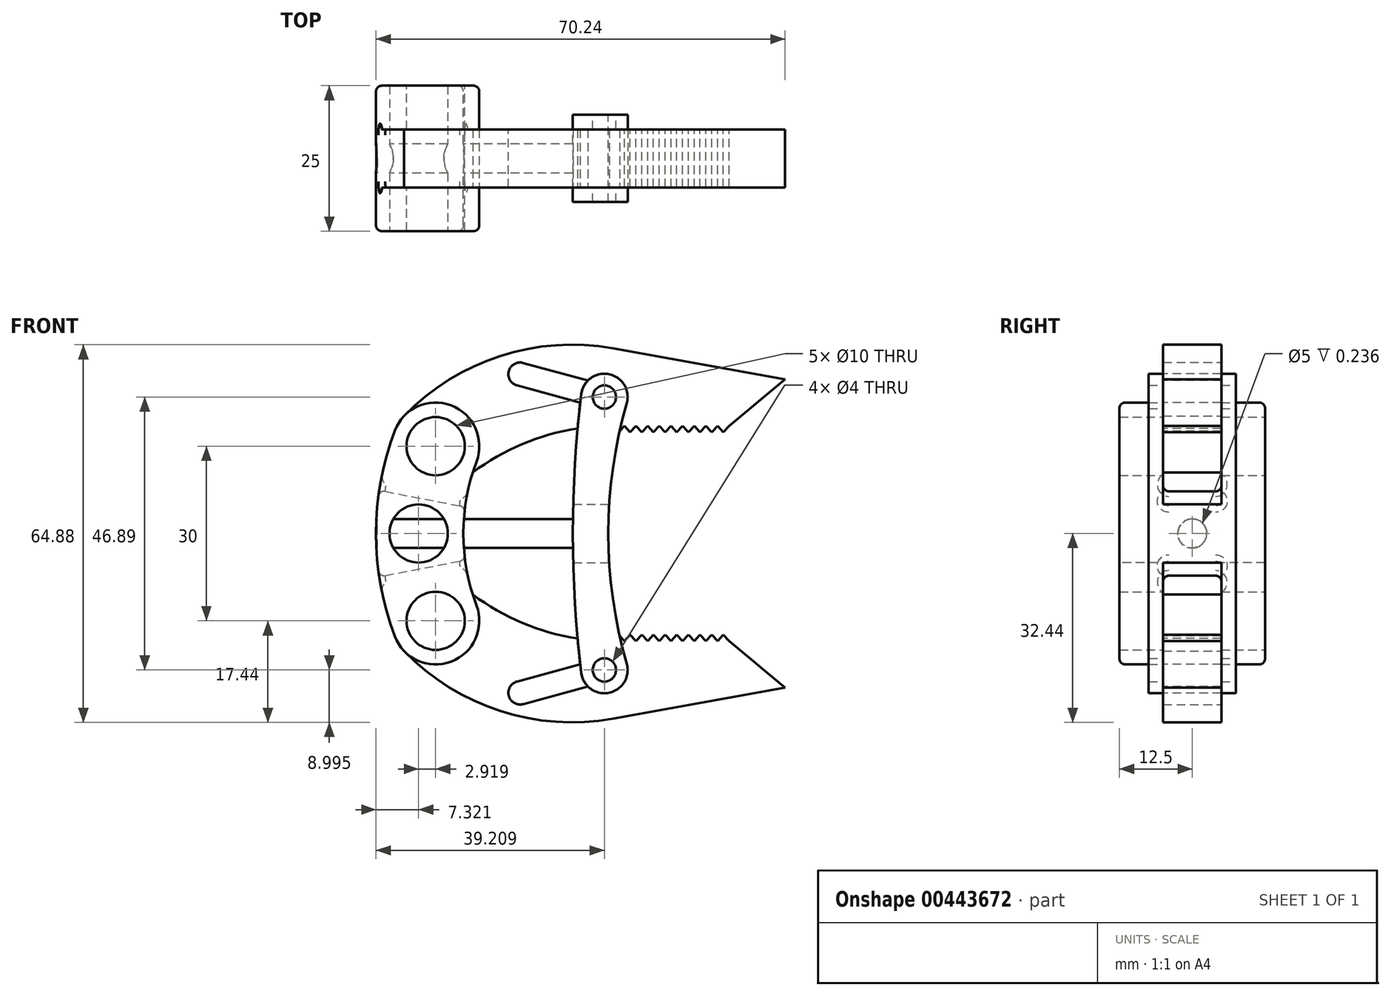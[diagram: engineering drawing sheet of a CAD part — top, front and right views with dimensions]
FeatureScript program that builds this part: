
annotation { "Feature Type Name" : "Feature", "Feature Type Description" : "" }
export const myFeature = defineFeature(function(context is Context, id is Id, definition is map)
    precondition{}
    {
        {
            var Q0;
            Q0=qCreatedBy(makeId("Front.planeOp"),FACE);
            var sketch = newSketch(context, id + "F0", { "sketchPlane" : qUnion([Q0])});
            skLineSegment(sketch, "E0", {"start": v(0, 15) * mm, "end": v(0, -15) * mm, "construction": true});
            skLineSegment(sketch, "E1", {"start": v(0, 0) * mm, "end": v(39.76, 0) * mm, "construction": true});
            skCircle(sketch, "E2", {"center": v(0, 15) * mm, "radius": 5 * mm});
            skCircle(sketch, "E3", {"center": v(0, -15) * mm, "radius": 5 * mm});
            skArc(sketch, "E4", {"start": v(-7.02, 17.65) * mm, "mid": v(-10.24, 0) * mm, "end": v(-7.02, -17.65) * mm});
            skCircle(sketch, "E5.0", {"center": v(0, 15) * mm, "radius": 7.5 * mm});
            skCircle(sketch, "E6.0", {"center": v(0, -15) * mm, "radius": 7.5 * mm});
            skArc(sketch, "E7", {"start": v(7.02, 12.35) * mm, "mid": v(4.76, 0) * mm, "end": v(7.02, -12.35) * mm});
            skSolve(sketch);
        }
        {
            var Q0;
            Q0=qCreatedBy(makeId("Front.planeOp"),FACE);
            var sketch = newSketch(context, id + "F1", { "sketchPlane" : qUnion([Q0])});
            skCircle(sketch, "E8.0", {"center": v(0, 15) * mm, "radius": 5 * mm});
            skArc(sketch, "E9", {"start": v(30.47, 31.81) * mm, "mid": v(11.08, 30.5) * mm, "end": v(-5.4, 20.2) * mm});
            skArc(sketch, "E10", {"start": v(30.4, 18.5) * mm, "mid": v(16.79, 16.12) * mm, "end": v(4.8, 9.24) * mm});
            skLineSegment(sketch, "E11", {"start": v(30.4, 18.5) * mm, "end": v(30.4, 18.5) * mm});
            skLineSegment(sketch, "E12", {"start": v(50.4, 18.5) * mm, "end": v(60, 26.5) * mm});
            skLineSegment(sketch, "E13", {"start": v(60, 26.5) * mm, "end": v(30.47, 31.81) * mm});
            skArc(sketch, "E14.0", {"start": v(-5.4, 20.2) * mm, "mid": v(-5.5, 9.9) * mm, "end": v(4.8, 9.24) * mm});
            skLineSegment(sketch, "E15", {"start": v(30.47, 31.81) * mm, "end": v(28.97, 23.45) * mm, "construction": true});
            skLineSegment(sketch, "E16", {"start": v(28.97, 23.45) * mm, "end": v(14.5, 27.38) * mm, "construction": true});
            skLineSegment(sketch, "E17", {"start": v(0, 0) * mm, "end": v(65.72, 0) * mm, "construction": true});
            skCircle(sketch, "E18", {"center": v(14.5, 27.38) * mm, "radius": 2 * mm});
            skCircle(sketch, "E19", {"center": v(28.97, 23.45) * mm, "radius": 2 * mm});
            skLineSegment(sketch, "E20", {"start": v(15.02, 29.3) * mm, "end": v(29.5, 25.38) * mm});
            skLineSegment(sketch, "E21", {"start": v(13.97, 25.45) * mm, "end": v(28.45, 21.51) * mm});
            skLineSegment(sketch, "E22", {"start": v(30.4, 18.5) * mm, "end": v(32.4, 18.5) * mm, "construction": true});
            skLineSegment(sketch, "E23", {"start": v(32.4, 18.5) * mm, "end": v(34.4, 18.5) * mm, "construction": true});
            skLineSegment(sketch, "E24", {"start": v(34.4, 18.5) * mm, "end": v(36.4, 18.5) * mm, "construction": true});
            skLineSegment(sketch, "E25", {"start": v(36.4, 18.5) * mm, "end": v(38.4, 18.5) * mm, "construction": true});
            skLineSegment(sketch, "E26", {"start": v(38.4, 18.5) * mm, "end": v(40.4, 18.5) * mm, "construction": true});
            skLineSegment(sketch, "E27", {"start": v(40.4, 18.5) * mm, "end": v(42.4, 18.5) * mm, "construction": true});
            skLineSegment(sketch, "E28", {"start": v(42.4, 18.5) * mm, "end": v(44.4, 18.5) * mm, "construction": true});
            skLineSegment(sketch, "E29", {"start": v(44.4, 18.5) * mm, "end": v(46.4, 18.5) * mm, "construction": true});
            skLineSegment(sketch, "E30", {"start": v(46.4, 18.5) * mm, "end": v(48.4, 18.5) * mm, "construction": true});
            skLineSegment(sketch, "E31", {"start": v(48.4, 18.5) * mm, "end": v(50.4, 18.5) * mm, "construction": true});
            skLineSegment(sketch, "E32", {"start": v(30.4, 18.5) * mm, "end": v(31.4, 17.39) * mm});
            skLineSegment(sketch, "E33", {"start": v(31.4, 17.39) * mm, "end": v(32.4, 18.5) * mm});
            skLineSegment(sketch, "E34", {"start": v(32.4, 18.5) * mm, "end": v(33.4, 17.39) * mm});
            skLineSegment(sketch, "E35", {"start": v(33.4, 17.39) * mm, "end": v(34.4, 18.5) * mm});
            skLineSegment(sketch, "E36", {"start": v(34.4, 18.5) * mm, "end": v(35.4, 17.39) * mm});
            skLineSegment(sketch, "E37", {"start": v(35.4, 17.39) * mm, "end": v(36.4, 18.5) * mm});
            skLineSegment(sketch, "E38", {"start": v(36.4, 18.5) * mm, "end": v(37.4, 17.39) * mm});
            skLineSegment(sketch, "E39", {"start": v(37.4, 17.39) * mm, "end": v(38.4, 18.5) * mm});
            skLineSegment(sketch, "E40", {"start": v(38.4, 18.5) * mm, "end": v(39.4, 17.39) * mm});
            skLineSegment(sketch, "E41", {"start": v(39.4, 17.39) * mm, "end": v(40.4, 18.5) * mm});
            skLineSegment(sketch, "E42", {"start": v(40.4, 18.5) * mm, "end": v(41.4, 17.39) * mm});
            skLineSegment(sketch, "E43", {"start": v(41.4, 17.39) * mm, "end": v(42.4, 18.5) * mm});
            skLineSegment(sketch, "E44", {"start": v(42.4, 18.5) * mm, "end": v(43.4, 17.39) * mm});
            skLineSegment(sketch, "E45", {"start": v(43.4, 17.39) * mm, "end": v(44.4, 18.5) * mm});
            skLineSegment(sketch, "E46", {"start": v(44.4, 18.5) * mm, "end": v(45.4, 17.39) * mm});
            skLineSegment(sketch, "E47", {"start": v(45.4, 17.39) * mm, "end": v(46.4, 18.5) * mm});
            skLineSegment(sketch, "E48", {"start": v(46.4, 18.5) * mm, "end": v(47.4, 17.39) * mm});
            skLineSegment(sketch, "E49", {"start": v(47.4, 17.39) * mm, "end": v(48.4, 18.5) * mm});
            skLineSegment(sketch, "E50", {"start": v(48.4, 18.5) * mm, "end": v(49.4, 17.39) * mm});
            skLineSegment(sketch, "E51", {"start": v(49.4, 17.39) * mm, "end": v(50.4, 18.5) * mm});
            skArc(sketch, "E52.MirrorCS", {"start": v(-5.4, -20.2) * mm, "mid": v(-5.5, -9.9) * mm, "end": v(4.8, -9.24) * mm});
            skLineSegment(sketch, "E53.MirrorCS", {"start": v(32.4, -18.5) * mm, "end": v(34.4, -18.5) * mm, "construction": true});
            skLineSegment(sketch, "E54.MirrorCS", {"start": v(30.4, -18.5) * mm, "end": v(32.4, -18.5) * mm, "construction": true});
            skLineSegment(sketch, "E55.MirrorCS", {"start": v(40.4, -18.5) * mm, "end": v(41.4, -17.39) * mm});
            skLineSegment(sketch, "E56.MirrorCS", {"start": v(44.4, -18.5) * mm, "end": v(46.4, -18.5) * mm, "construction": true});
            skLineSegment(sketch, "E57.MirrorCS", {"start": v(38.4, -18.5) * mm, "end": v(40.4, -18.5) * mm, "construction": true});
            skLineSegment(sketch, "E58.MirrorCS", {"start": v(46.4, -18.5) * mm, "end": v(48.4, -18.5) * mm, "construction": true});
            skLineSegment(sketch, "E59.MirrorCS", {"start": v(41.4, -17.39) * mm, "end": v(42.4, -18.5) * mm});
            skLineSegment(sketch, "E60.MirrorCS", {"start": v(36.4, -18.5) * mm, "end": v(38.4, -18.5) * mm, "construction": true});
            skLineSegment(sketch, "E61.MirrorCS", {"start": v(40.4, -18.5) * mm, "end": v(42.4, -18.5) * mm, "construction": true});
            skLineSegment(sketch, "E62.MirrorCS", {"start": v(34.4, -18.5) * mm, "end": v(36.4, -18.5) * mm, "construction": true});
            skLineSegment(sketch, "E63.MirrorCS", {"start": v(42.4, -18.5) * mm, "end": v(44.4, -18.5) * mm, "construction": true});
            skLineSegment(sketch, "E64.MirrorCS", {"start": v(30.4, -18.5) * mm, "end": v(31.4, -17.39) * mm});
            skLineSegment(sketch, "E65.MirrorCS", {"start": v(34.4, -18.5) * mm, "end": v(35.4, -17.39) * mm});
            skLineSegment(sketch, "E66.MirrorCS", {"start": v(38.4, -18.5) * mm, "end": v(39.4, -17.39) * mm});
            skLineSegment(sketch, "E67.MirrorCS", {"start": v(48.4, -18.5) * mm, "end": v(50.4, -18.5) * mm, "construction": true});
            skLineSegment(sketch, "E68.MirrorCS", {"start": v(32.4, -18.5) * mm, "end": v(33.4, -17.39) * mm});
            skLineSegment(sketch, "E69.MirrorCS", {"start": v(48.4, -18.5) * mm, "end": v(49.4, -17.39) * mm});
            skLineSegment(sketch, "E70.MirrorCS", {"start": v(44.4, -18.5) * mm, "end": v(45.4, -17.39) * mm});
            skLineSegment(sketch, "E71.MirrorCS", {"start": v(33.4, -17.39) * mm, "end": v(34.4, -18.5) * mm});
            skLineSegment(sketch, "E72.MirrorCS", {"start": v(31.4, -17.39) * mm, "end": v(32.4, -18.5) * mm});
            skLineSegment(sketch, "E73.MirrorCS", {"start": v(43.4, -17.39) * mm, "end": v(44.4, -18.5) * mm});
            skLineSegment(sketch, "E74.MirrorCS", {"start": v(35.4, -17.39) * mm, "end": v(36.4, -18.5) * mm});
            skLineSegment(sketch, "E75.MirrorCS", {"start": v(37.4, -17.39) * mm, "end": v(38.4, -18.5) * mm});
            skLineSegment(sketch, "E76.MirrorCS", {"start": v(45.4, -17.39) * mm, "end": v(46.4, -18.5) * mm});
            skLineSegment(sketch, "E77.MirrorCS", {"start": v(46.4, -18.5) * mm, "end": v(47.4, -17.39) * mm});
            skLineSegment(sketch, "E78.MirrorCS", {"start": v(39.4, -17.39) * mm, "end": v(40.4, -18.5) * mm});
            skLineSegment(sketch, "E79.MirrorCS", {"start": v(42.4, -18.5) * mm, "end": v(43.4, -17.39) * mm});
            skLineSegment(sketch, "E80.MirrorCS", {"start": v(49.4, -17.39) * mm, "end": v(50.4, -18.5) * mm});
            skLineSegment(sketch, "E81.MirrorCS", {"start": v(47.4, -17.39) * mm, "end": v(48.4, -18.5) * mm});
            skLineSegment(sketch, "E82.MirrorCS", {"start": v(36.4, -18.5) * mm, "end": v(37.4, -17.39) * mm});
            skLineSegment(sketch, "E83.MirrorCS", {"start": v(30.47, -31.81) * mm, "end": v(28.97, -23.45) * mm, "construction": true});
            skLineSegment(sketch, "E84.MirrorCS", {"start": v(28.97, -23.45) * mm, "end": v(14.5, -27.38) * mm, "construction": true});
            skCircle(sketch, "E85.MirrorC", {"center": v(14.5, -27.38) * mm, "radius": 2 * mm});
            skCircle(sketch, "E86.MirrorC", {"center": v(28.97, -23.45) * mm, "radius": 2 * mm});
            skLineSegment(sketch, "E87.MirrorCS", {"start": v(15.02, -29.3) * mm, "end": v(29.5, -25.38) * mm});
            skLineSegment(sketch, "E88.MirrorCS", {"start": v(13.97, -25.45) * mm, "end": v(28.45, -21.51) * mm});
            skCircle(sketch, "E89.MirrorC", {"center": v(0, -15) * mm, "radius": 5 * mm});
            skArc(sketch, "E90.MirrorCS", {"start": v(30.4, -18.5) * mm, "mid": v(16.79, -16.12) * mm, "end": v(4.8, -9.24) * mm});
            skLineSegment(sketch, "E91.MirrorCS", {"start": v(60, -26.5) * mm, "end": v(30.47, -31.81) * mm});
            skArc(sketch, "E92.MirrorCS", {"start": v(30.47, -31.81) * mm, "mid": v(11.08, -30.5) * mm, "end": v(-5.4, -20.2) * mm});
            skLineSegment(sketch, "E93.MirrorCS", {"start": v(50.4, -18.5) * mm, "end": v(60, -26.5) * mm});
            skSolve(sketch);
        }
        {
            var Q0;
            Q0 = qSketchRegion(id + "F0", true);
            extrude(context, id + "F2", {"entities" : qUnion([Q0]), "endBound" : BoundingType.SYMMETRIC, "depth" : 25 * mm});
        }
        {
            var Q0;
            Q0 = qSketchRegion(id + "F1", true);
            extrude(context, id + "F3", {"entities" : qUnion([Q0]), "endBound" : BoundingType.SYMMETRIC, "depth" : 10 * mm});
        }
        {
            var Q0;
            Q0=makeQuery(id+"F2.opExtrude","CAP_FACE",FACE,{"disambiguationData":[OSD([sQuery(id+"F0.wireOp",EDGE,"E2"),sQuery(id+"F0.wireOp",EDGE,"E3"),sQuery(id+"F0.wireOp",EDGE,"E4"),sQuery(id+"F0.wireOp",EDGE,"E5.0"),sQuery(id+"F0.wireOp",EDGE,"E6.0"),sQuery(id+"F0.wireOp",EDGE,"E7")])],"isStart":false});
            var sketch = newSketch(context, id + "F4", { "sketchPlane" : qUnion([Q0])});
            skCircle(sketch, "E94", {"center": v(0, 15) * mm, "radius": 5 * mm});
            skCircle(sketch, "E95", {"center": v(0, -15) * mm, "radius": 5 * mm});
            skArc(sketch, "E96", {"start": v(0, 15) * mm, "mid": v(-2.92, 0) * mm, "end": v(0, -15) * mm, "construction": true});
            skCircle(sketch, "E97", {"center": v(-2.92, 0) * mm, "radius": 5 * mm});
            skSolve(sketch);
        }
        {
            var Q0;
            Q0=makeQuery(id+"F4.imprint","IMPRINT",FACE,{"disambiguationData":[TD([[makeQuery(id+"F4.imprint","IMPRINT",EDGE,{"derivedFrom":sQuery(id+"F4.wireOp",EDGE,"E97")}),1.0]])]});
            extrude(context, id + "F5", {"entities" : qUnion([Q0]), "operationType" : NewBodyOperationType.REMOVE, "endBound" : BoundingType.THROUGH_ALL, "oppositeDirection" : true, "depth" : 25 * mm});
        }
        {
            var Q0;
            Q0=qCreatedBy(makeId("Front.planeOp"),FACE);
            var sketch = newSketch(context, id + "F6", { "sketchPlane" : qUnion([Q0])});
            skCircle(sketch, "E98", {"center": v(-2.92, 0) * mm, "radius": 5 * mm});
            skCircle(sketch, "E99", {"center": v(0, 15) * mm, "radius": 5 * mm});
            skCircle(sketch, "E100.0", {"center": v(-2.92, 0) * mm, "radius": 6 * mm, "construction": true});
            skCircle(sketch, "E101", {"center": v(0, 15) * mm, "radius": 9.28 * mm, "construction": true});
            skLineSegment(sketch, "E102", {"start": v(0, 15) * mm, "end": v(-2.92, 0) * mm, "construction": true});
            skLineSegment(sketch, "E103", {"start": v(-2.92, 0) * mm, "end": v(25, 0) * mm, "construction": true});
            skLineSegment(sketch, "E104", {"start": v(-9.68, 7.43) * mm, "end": v(5.06, 4.56) * mm});
            skLineSegment(sketch, "E105.MirrorCS", {"start": v(-9.68, -7.43) * mm, "end": v(5.06, -4.56) * mm});
            skArc(sketch, "E106", {"start": v(7.02, 12.35) * mm, "mid": v(5.82, 8.51) * mm, "end": v(5.06, 4.56) * mm});
            skArc(sketch, "E107", {"start": v(-7.02, 17.65) * mm, "mid": v(-8.62, 12.6) * mm, "end": v(-9.68, 7.43) * mm});
            skArc(sketch, "E108.MirrorCS", {"start": v(7.02, -12.35) * mm, "mid": v(5.82, -8.51) * mm, "end": v(5.06, -4.56) * mm});
            skArc(sketch, "E109.MirrorCS", {"start": v(-7.02, -17.65) * mm, "mid": v(-8.62, -12.6) * mm, "end": v(-9.68, -7.43) * mm});
            skArc(sketch, "E110", {"start": v(-7.02, -17.65) * mm, "mid": v(2.65, -22.02) * mm, "end": v(7.02, -12.35) * mm});
            skArc(sketch, "E111", {"start": v(7.02, 12.35) * mm, "mid": v(2.65, 22.02) * mm, "end": v(-7.02, 17.65) * mm});
            skSolve(sketch);
        }
        {
            var Q0;
            Q0 = qSketchRegion(id + "F6", true);
            var Q1;
            Q1=sQuery(id+"F6.wireOp",EDGE,"E104");
            var Q2;
            Q2=sQuery(id+"F6.wireOp",EDGE,"E107");
            var Q3;
            Q3=sQuery(id+"F6.wireOp",EDGE,"E111");
            var Q4;
            Q4=sQuery(id+"F6.wireOp",EDGE,"E106");
            var Q5;
            Q5=sQuery(id+"F6.wireOp",EDGE,"E108.MirrorCS");
            var Q6;
            Q6=sQuery(id+"F6.wireOp",EDGE,"E110");
            var Q7;
            Q7=sQuery(id+"F6.wireOp",EDGE,"E105.MirrorCS");
            var Q8;
            Q8=sQuery(id+"F6.wireOp",EDGE,"E109.MirrorCS");
            extrude(context, id + "F7", {"entities" : qUnion([Q0]), "operationType" : NewBodyOperationType.REMOVE, "surfaceEntities" : qUnion([Q1, Q2, Q3, Q4, Q5, Q6, Q7, Q8]), "endBound" : BoundingType.SYMMETRIC, "oppositeDirection" : true, "depth" : 10 * mm});
        }
        {
            var Q0;
            Q0=qCreatedBy(makeId("Right.planeOp"),FACE);
            var sketch = newSketch(context, id + "F8", { "sketchPlane" : qUnion([Q0])});
            skCircle(sketch, "E112", {"center": v(0, 0) * mm, "radius": 2.5 * mm});
            skSolve(sketch);
        }
        {
            var Q0;
            Q0 = qSketchRegion(id + "F8", true);
            extrude(context, id + "F9", {"entities" : qUnion([Q0]), "operationType" : NewBodyOperationType.REMOVE, "endBound" : BoundingType.THROUGH_ALL, "depth" : 25 * mm, "hasSecondDirection" : true, "secondDirectionBound" : SecondDirectionBoundingType.THROUGH_ALL, "secondDirectionOppositeDirection" : true, "secondDirectionDepth" : 25 * mm});
        }
        {
            var Q0;
            Q0 = qSketchRegion(id + "F8", true);
            extrude(context, id + "F10", {"entities" : qUnion([Q0]), "depth" : 27 * mm, "hasSecondDirection" : true, "secondDirectionOppositeDirection" : true, "secondDirectionDepth" : 10 * mm});
        }
        {
            var Q0;
            Q0=qCreatedBy(makeId("Front.planeOp"),FACE);
            var sketch = newSketch(context, id + "F11", { "sketchPlane" : qUnion([Q0])});
            skCircle(sketch, "E113", {"center": v(28.97, 23.45) * mm, "radius": 2 * mm});
            skCircle(sketch, "E114", {"center": v(28.97, -23.45) * mm, "radius": 2 * mm});
            skCircle(sketch, "E115", {"center": v(28.97, 23.45) * mm, "radius": 4 * mm});
            skCircle(sketch, "E116", {"center": v(28.97, -23.45) * mm, "radius": 4 * mm});
            skArc(sketch, "E117", {"start": v(32.81, 22.33) * mm, "mid": v(29.63, 0) * mm, "end": v(32.81, -22.33) * mm});
            skArc(sketch, "E118", {"start": v(25, 23.92) * mm, "mid": v(23.56, 0) * mm, "end": v(25, -23.92) * mm});
            skLineSegment(sketch, "E119", {"start": v(0.5, 0) * mm, "end": v(51.97, 0) * mm, "construction": true});
            skLineSegment(sketch, "E120", {"start": v(28.97, 23.45) * mm, "end": v(28.97, -23.45) * mm, "construction": true});
            skSolve(sketch);
        }
        {
            var Q0;
            Q0 = qSketchRegion(id + "F11", true);
            extrude(context, id + "F12", {"entities" : qUnion([Q0]), "endBound" : BoundingType.SYMMETRIC, "depth" : 15 * mm});
        }
        {
            var Q0;
            Q0=qCreatedBy(makeId("Front.planeOp"),FACE);
            var sketch = newSketch(context, id + "F13", { "sketchPlane" : qUnion([Q0])});
            skLineSegment(sketch, "E121", {"start": v(23.62, 5) * mm, "end": v(29.79, 5) * mm});
            skLineSegment(sketch, "E122", {"start": v(23.62, -5) * mm, "end": v(29.79, -5) * mm});
            skLineSegment(sketch, "E123", {"start": v(14.44, 0) * mm, "end": v(35.78, 0) * mm, "construction": true});
            skArc(sketch, "E124.0.0", {"start": v(32.81, 22.33) * mm, "mid": v(29.77, 27.36) * mm, "end": v(25, 23.92) * mm});
            skArc(sketch, "E124.0.1", {"start": v(25, 23.92) * mm, "mid": v(24.09, 14.48) * mm, "end": v(23.62, 5) * mm});
            skArc(sketch, "E124.0.2", {"start": v(25, -23.92) * mm, "mid": v(29.77, -27.36) * mm, "end": v(32.81, -22.33) * mm});
            skArc(sketch, "E124.0.3", {"start": v(32.81, -22.33) * mm, "mid": v(30.82, -13.75) * mm, "end": v(29.79, -5) * mm});
            skArc(sketch, "E125.trimOffspring", {"start": v(29.79, 5) * mm, "mid": v(30.82, 13.75) * mm, "end": v(32.81, 22.33) * mm});
            skArc(sketch, "E126.trimOffspring", {"start": v(23.62, -5) * mm, "mid": v(24.09, -14.48) * mm, "end": v(25, -23.92) * mm});
            skSolve(sketch);
        }
        {
            var Q0;
            Q0 = qSketchRegion(id + "F13", true);
            var Q1;
            Q1=sQuery(id+"F13.wireOp",EDGE,"E124.0.1");
            var Q2;
            Q2=sQuery(id+"F13.wireOp",EDGE,"E125.trimOffspring");
            var Q3;
            Q3=sQuery(id+"F13.wireOp",EDGE,"E121");
            var Q4;
            Q4=sQuery(id+"F13.wireOp",EDGE,"E124.0.0");
            var Q5;
            Q5=sQuery(id+"F13.wireOp",EDGE,"E126.trimOffspring");
            var Q6;
            Q6=sQuery(id+"F13.wireOp",EDGE,"E124.0.3");
            var Q7;
            Q7=sQuery(id+"F13.wireOp",EDGE,"E124.0.2");
            var Q8;
            Q8=sQuery(id+"F13.wireOp",EDGE,"E122");
            extrude(context, id + "F14", {"entities" : qUnion([Q0]), "operationType" : NewBodyOperationType.REMOVE, "surfaceEntities" : qUnion([Q1, Q2, Q3, Q4, Q5, Q6, Q7, Q8]), "endBound" : BoundingType.SYMMETRIC, "oppositeDirection" : true, "depth" : 10 * mm});
        }
        {
            var Q0;
            Q0=makeQuery(id+"F2.opExtrude","CAP_EDGE",EDGE,{"disambiguationData":[OSD([sQuery(id+"F0.wireOp",EDGE,"E7")])],"isStart":true});
            var Q1;
            Q1=makeQuery(id+"F2.opExtrude","CAP_EDGE",EDGE,{"disambiguationData":[OSD([sQuery(id+"F0.wireOp",EDGE,"E7")])],"isStart":false});
            var Q2;
            Q2=makeQuery(id+"F7.boolean.opBoolean","COPY",FACE,{"derivedFrom":makeQuery(id+"F7.opExtrude","SWEPT_FACE",FACE,{"disambiguationData":[OSD([sQuery(id+"F6.wireOp",EDGE,"E104")])]})});
            var Q3;
            Q3=makeQuery(id+"F7.boolean.opBoolean","COPY",FACE,{"derivedFrom":makeQuery(id+"F7.opExtrude","SWEPT_FACE",FACE,{"disambiguationData":[OSD([sQuery(id+"F6.wireOp",EDGE,"E105.MirrorCS")])]})});
            var Q4;
            Q4=makeQuery(id+"F7.boolean.opBoolean","COPY",EDGE,{"derivedFrom":makeQuery(id+"F7.opExtrude","CAP_EDGE",EDGE,{"disambiguationData":[OSD([sQuery(id+"F6.wireOp",EDGE,"E106")])],"isStart":false})});
            fillet(context, id + "F15", {"entities" : qUnion([Q0, Q1, Q2, Q3, Q4]), "radius" : 1 * mm, "tangentPropagation" : true, "allowEdgeOverflow" : false});
        }
        {
            var Q0;
            Q0=makeQuery(id+"F10.opExtrude","SWEPT_BODY",BODY,{"disambiguationData":[OSD([sQuery(id+"F8.wireOp",EDGE,"E112")])]});
            deleteBodies(context, id + "F16", {"entities" : qUnion([Q0])});
        }
        {
            var Q0;
            Q0=qCreatedBy(makeId("Right.planeOp"),FACE);
            var sketch = newSketch(context, id + "F17", { "sketchPlane" : qUnion([Q0])});
            skCircle(sketch, "E127", {"center": v(0, 0) * mm, "radius": 2.5 * mm});
            skSolve(sketch);
        }
        {
            var Q0;
            Q0 = qSketchRegion(id + "F17", true);
            extrude(context, id + "F18", {"entities" : qUnion([Q0]), "operationType" : NewBodyOperationType.ADD, "depth" : 27 * mm, "hasSecondDirection" : true, "secondDirectionOppositeDirection" : true, "secondDirectionDepth" : 10 * mm});
        }
    });
